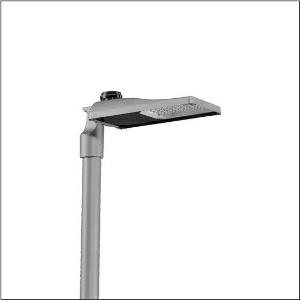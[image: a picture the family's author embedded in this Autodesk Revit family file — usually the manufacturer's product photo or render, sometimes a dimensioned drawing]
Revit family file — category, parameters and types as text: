
# Revit family: streetlight_sl_31_mini___st1_0a_5xh2d35n08ha_d2d6
name_source: partatom
category: Lighting Fixtures
units: mm (PartAtom-declared; Revit-internal decimal feet)

## family parameters
Cut with Voids When Loaded = No
Host = Face
Light Source = No
Part Type = Normal
Room Calculation Point = No
Round Connector Dimension = Use Diameter
Shared = No

## types (1)
- --- (1 x LED, 9240 lm, 68.3 W, 3000K)
    Apparent Load = 68 VA
    CIE Flux Codes = 37 72 97 100 100
    Color Rendering = 70
    Color Temperature = 3000K
    Default Elevation = 1800 mm
    Description = Streetlight SL 31 mini NEMA (7pin), Desk-Remote mast luminaire for post-top, side-entry; light control with lens of PMMA; light distribution: ST1.0a, direct asymmetric distribution, for standard-compliant lighting for roads and squares; LED: luminous flux: 9.240lm, light colour: 730, colour temperature: 3000K; luminous efficacy: 135,3lm/W; control: pre-setting: linear dimming characteristic, flexible luminous flux parameterisation, time-dependent luminous flux control, constant luminous flux control, intelligent temperature release in ECG and LED module, overheat protection; luminaire housing, of diecast aluminium, SITECO metallic grey (DB 702S), corrosivity category C5 high according to DIN EN ISO 12944; cover of toughened safety glass, transparent, mast flange of diecast aluminium, SITECO metallic grey (DB 702S), spigot size: 76/60mm, mast flange included unmounted; cable length: 8,5m, connection cable pre-assembled; mains connection: 220..240V, AC, 50/60Hz; power consumption (at start of service life): 68,3W / (at end of service life): 74,8W / (with reduced operation 50%): 29,7W; protection rating (complete): IP66; insulation class (complete): insulation class I (protective earthing); impact resistance: IK10; certification: CE, ENEC, ENEC+, VDE, UKCA; permissible operating ambient temperature for outdoor applications: -40..+50°C; packaging unit: 1 piece

Light Distribution: ST1.0a
    Height = 76 mm
    Lamp = 1 x LED
    Lamp Light Flux = 9240 lm
    Lamp Power = 68.3 W
    Lamp count = 1
    Length = 547 mm
    Luminous efficacy = 135 lm/W
    Manufacturer = Siteco
    ModVariant = No
    Model = 5XH2D35N08HA
    Number of Poles = 1
    OnlyDefault = Yes
    Power Factor = 1
    Product Name = Streetlight SL 31 mini | ST1.0a
    Product group = mast luminaire | pylon top
    ProductGroupID = 6100
    Protection Class = Protection class I
    Protection Degree = IP 66
    RLX_Detail_Level = 1
    RLX_Emergency_Light_Flux = 0 lm
    RLX_Emergency_Type = 0
    RLX_Emergency_Type_DB = No
    RlxData = <blob elided: 40077 chars, md5=ab91332f>
    Socket = socket
    Standby Power = 0 W
    System Light Flux = 9240 lm
    System Power = 68 W
    Type Comments = factory setting: luminous flux: 100 % | dim-lin: 254 | 693 mA
    Type Image = l_1300322.jpg
    URL = http://relux.com
    VarID = @adj_061255
    Voltage = 0 V
    Weight = 0.00 kg
    Width = 265 mm

## geometry (parser evidence)
native form markers: Blend x4, Sweep x10
no freeform markers — native parametric forms only
